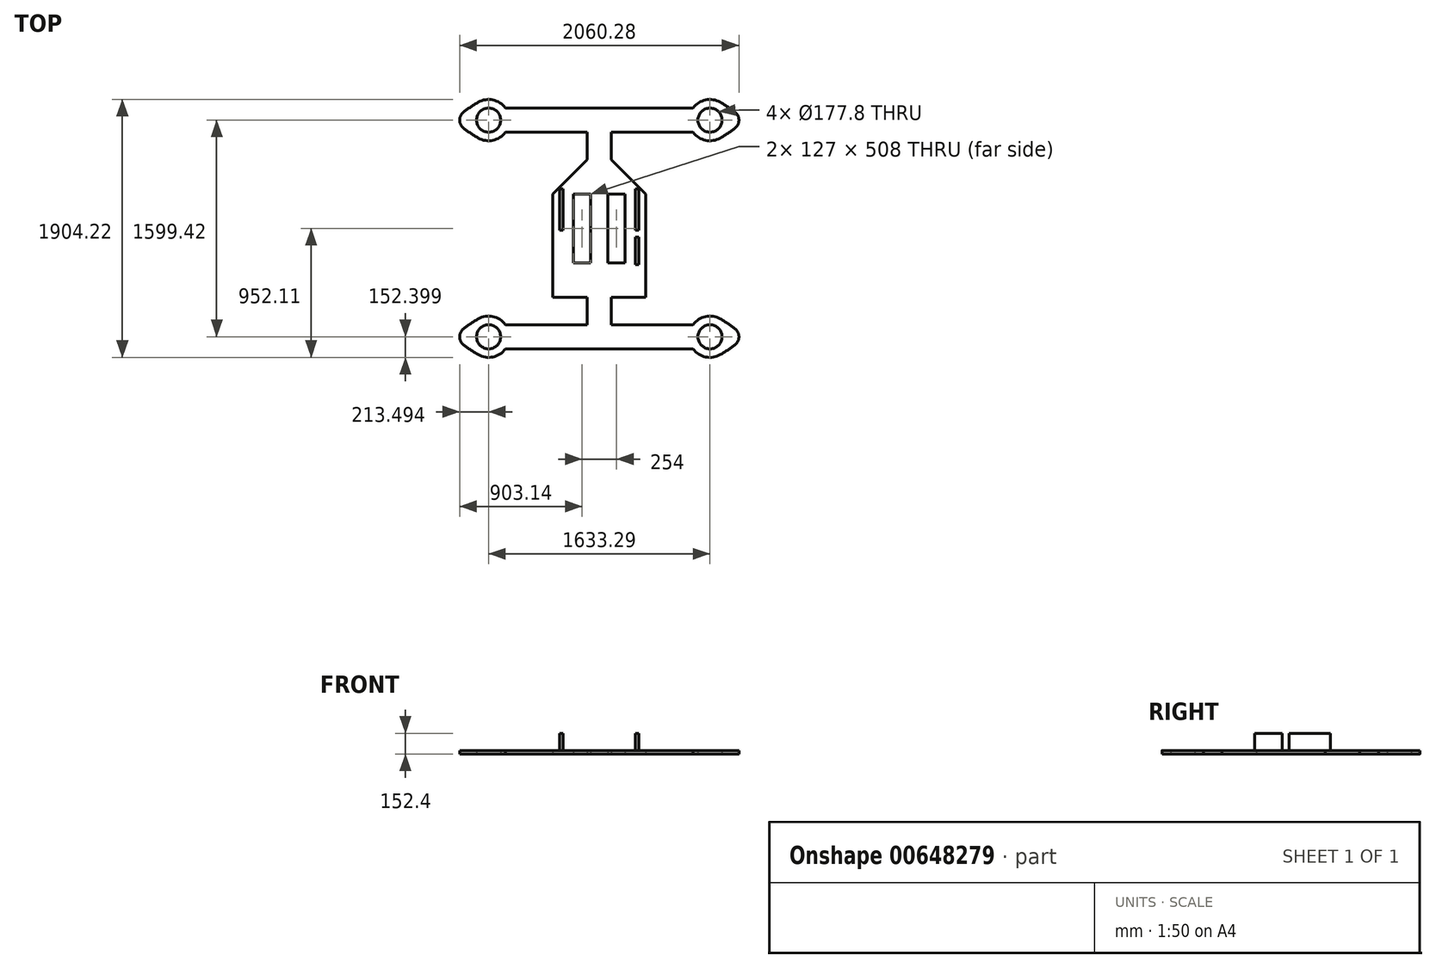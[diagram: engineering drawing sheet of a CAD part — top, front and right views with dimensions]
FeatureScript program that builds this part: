
annotation { "Feature Type Name" : "Feature", "Feature Type Description" : "" }
export const myFeature = defineFeature(function(context is Context, id is Id, definition is map)
    precondition{}
    {
        {
            var Q0;
            Q0=qCreatedBy(makeId("Top.planeOp"),FACE);
            var sketch = newSketch(context, id + "F0", { "sketchPlane" : qUnion([Q0])});
            skLineSegment(sketch, "E0.bottom", {"start": v(-816.65, 799.71) * mm, "end": v(816.65, 799.71) * mm, "construction": true});
            skLineSegment(sketch, "E0.top", {"start": v(-816.65, -799.71) * mm, "end": v(816.65, -799.71) * mm, "construction": true});
            skLineSegment(sketch, "E0.left", {"start": v(-816.65, 799.71) * mm, "end": v(-816.65, -799.71) * mm, "construction": true});
            skLineSegment(sketch, "E0.right", {"start": v(816.65, 799.71) * mm, "end": v(816.65, -799.71) * mm, "construction": true});
            skCircle(sketch, "E1", {"center": v(-816.65, 799.71) * mm, "radius": 88.9 * mm});
            skCircle(sketch, "E2", {"center": v(816.65, 799.71) * mm, "radius": 88.9 * mm});
            skCircle(sketch, "E3", {"center": v(816.65, -799.71) * mm, "radius": 88.9 * mm});
            skCircle(sketch, "E4", {"center": v(-816.65, -799.71) * mm, "radius": 88.9 * mm});
            skArc(sketch, "E5", {"start": v(-892.85, 667.73) * mm, "mid": v(-784.55, 650.73) * mm, "end": v(-692.86, 710.81) * mm});
            skArc(sketch, "E6", {"start": v(892.85, 931.7) * mm, "mid": v(784.55, 948.7) * mm, "end": v(692.86, 888.61) * mm});
            skArc(sketch, "E7", {"start": v(892.85, -667.73) * mm, "mid": v(784.55, -650.73) * mm, "end": v(692.86, -710.81) * mm});
            skArc(sketch, "E8", {"start": v(-892.85, -931.7) * mm, "mid": v(-784.55, -948.7) * mm, "end": v(-692.86, -888.61) * mm});
            skPoint(sketch, "E9.endSnap0", {"position": v(816.65, 0) * mm});
            skLineSegment(sketch, "E10", {"start": v(-692.86, 888.61) * mm, "end": v(692.86, 888.61) * mm});
            skLineSegment(sketch, "E11", {"start": v(-692.86, -888.61) * mm, "end": v(692.86, -888.61) * mm});
            skLineSegment(sketch, "E12.top", {"start": v(-342.9, -508) * mm, "end": v(-88.9, -508) * mm});
            skLineSegment(sketch, "E12.left", {"start": v(-342.9, 254) * mm, "end": v(-342.9, -508) * mm});
            skLineSegment(sketch, "E12.right", {"start": v(342.9, 254) * mm, "end": v(342.9, -508) * mm});
            skLineSegment(sketch, "E13", {"start": v(-88.9, 710.81) * mm, "end": v(-88.9, 508) * mm});
            skPoint(sketch, "E13.endSnap0", {"position": v(0, 508) * mm});
            skLineSegment(sketch, "E14", {"start": v(-88.9, -508) * mm, "end": v(-88.9, -710.81) * mm});
            skLineSegment(sketch, "E15", {"start": v(-88.9, 710.81) * mm, "end": v(-692.86, 710.81) * mm});
            skLineSegment(sketch, "E16", {"start": v(-88.9, -710.81) * mm, "end": v(-692.86, -710.81) * mm});
            skLineSegment(sketch, "E17", {"start": v(0, 0) * mm, "end": v(342.9, 0) * mm, "construction": true});
            skLineSegment(sketch, "E18", {"start": v(0, 0) * mm, "end": v(0, 1037.77) * mm, "construction": true});
            skLineSegment(sketch, "E19.MirrorCS", {"start": v(88.9, 710.81) * mm, "end": v(88.9, 508) * mm});
            skLineSegment(sketch, "E20.MirrorCS", {"start": v(88.9, 710.81) * mm, "end": v(692.86, 710.81) * mm});
            skLineSegment(sketch, "E21.MirrorCS", {"start": v(88.9, -710.81) * mm, "end": v(692.86, -710.81) * mm});
            skLineSegment(sketch, "E22.MirrorCS", {"start": v(88.9, -508) * mm, "end": v(88.9, -710.81) * mm});
            skLineSegment(sketch, "E23.trimOffspring", {"start": v(88.9, -508) * mm, "end": v(342.9, -508) * mm});
            skArc(sketch, "E24", {"start": v(1000.09, 860.35) * mm, "mid": v(947.6, 897.72) * mm, "end": v(892.85, 931.7) * mm});
            skArc(sketch, "E25", {"start": v(892.85, 667.73) * mm, "mid": v(947.6, 701.7) * mm, "end": v(1000.09, 739.07) * mm});
            skPoint(sketch, "E26.visualSharp", {"position": v(1072.53, 799.71) * mm});
            skArc(sketch, "E26.filletArc", {"start": v(1000.09, 739.07) * mm, "mid": v(1030.14, 799.71) * mm, "end": v(1000.09, 860.35) * mm});
            skArc(sketch, "E27.MirrorCS", {"start": v(-892.85, 667.73) * mm, "mid": v(-947.6, 701.7) * mm, "end": v(-1000.09, 739.07) * mm});
            skArc(sketch, "E28.MirrorCS", {"start": v(-1000.09, 739.07) * mm, "mid": v(-1030.14, 799.71) * mm, "end": v(-1000.09, 860.35) * mm});
            skArc(sketch, "E29.MirrorCS", {"start": v(-1000.09, 860.35) * mm, "mid": v(-947.6, 897.72) * mm, "end": v(-892.85, 931.7) * mm});
            skArc(sketch, "E30.MirrorCS", {"start": v(1000.09, -860.35) * mm, "mid": v(947.6, -897.72) * mm, "end": v(892.85, -931.7) * mm});
            skArc(sketch, "E31.MirrorCS", {"start": v(1000.09, -739.07) * mm, "mid": v(1030.14, -799.71) * mm, "end": v(1000.09, -860.35) * mm});
            skArc(sketch, "E32.MirrorCS", {"start": v(892.85, -667.73) * mm, "mid": v(947.6, -701.7) * mm, "end": v(1000.09, -739.07) * mm});
            skArc(sketch, "E33.MirrorCS", {"start": v(-1000.09, -860.35) * mm, "mid": v(-947.6, -897.72) * mm, "end": v(-892.85, -931.7) * mm});
            skArc(sketch, "E34.MirrorCS", {"start": v(-1000.09, -739.07) * mm, "mid": v(-1030.14, -799.71) * mm, "end": v(-1000.09, -860.35) * mm});
            skArc(sketch, "E35.MirrorCS", {"start": v(-892.85, -667.73) * mm, "mid": v(-947.6, -701.7) * mm, "end": v(-1000.09, -739.07) * mm});
            skLineSegment(sketch, "E36.bottom", {"start": v(-190.5, 254) * mm, "end": v(-63.5, 254) * mm});
            skLineSegment(sketch, "E36.top", {"start": v(-190.5, -254) * mm, "end": v(-63.5, -254) * mm});
            skLineSegment(sketch, "E36.left", {"start": v(-190.5, 254) * mm, "end": v(-190.5, -254) * mm});
            skLineSegment(sketch, "E36.right", {"start": v(-63.5, 254) * mm, "end": v(-63.5, -254) * mm});
            skLineSegment(sketch, "E37.bottom", {"start": v(63.5, 254) * mm, "end": v(190.5, 254) * mm});
            skLineSegment(sketch, "E37.top", {"start": v(63.5, -254) * mm, "end": v(190.5, -254) * mm});
            skLineSegment(sketch, "E37.left", {"start": v(63.5, 254) * mm, "end": v(63.5, -254) * mm});
            skLineSegment(sketch, "E37.right", {"start": v(190.5, 254) * mm, "end": v(190.5, -254) * mm});
            skLineSegment(sketch, "E38", {"start": v(88.9, 508) * mm, "end": v(342.9, 254) * mm});
            skLineSegment(sketch, "E39", {"start": v(-88.9, 508) * mm, "end": v(-342.9, 254) * mm});
            skPoint(sketch, "E40.orphan", {"position": v(-342.9, 508) * mm});
            skPoint(sketch, "E41.orphan", {"position": v(342.9, 508) * mm});
            skLineSegment(sketch, "E42.trimOffspring", {"start": v(816.65, 0) * mm, "end": v(1418.73, 0) * mm, "construction": true});
            skArc(sketch, "E43.trimOffspring", {"start": v(-692.86, 888.61) * mm, "mid": v(-784.55, 948.7) * mm, "end": v(-892.85, 931.7) * mm});
            skArc(sketch, "E44.trimOffspring", {"start": v(692.86, 710.81) * mm, "mid": v(784.55, 650.73) * mm, "end": v(892.85, 667.73) * mm});
            skArc(sketch, "E45.trimOffspring", {"start": v(692.86, -888.61) * mm, "mid": v(784.55, -948.7) * mm, "end": v(892.85, -931.7) * mm});
            skArc(sketch, "E46.trimOffspring", {"start": v(-692.86, -710.81) * mm, "mid": v(-784.55, -650.73) * mm, "end": v(-892.85, -667.73) * mm});
            skSolve(sketch);
        }
        {
            var Q0;
            Q0 = qSketchRegion(id + "F0", true);
            extrude(context, id + "F1", {"entities" : qUnion([Q0]), "depth" : 25.4 * mm, "offsetDistance" : 25.4 * mm});
        }
        {
            var Q0;
            Q0=makeQuery(id+"F1.opExtrude","CAP_FACE",FACE,{"disambiguationData":[OSD([sQuery(id+"F0.wireOp",EDGE,"E1"),sQuery(id+"F0.wireOp",EDGE,"E2"),sQuery(id+"F0.wireOp",EDGE,"E3"),sQuery(id+"F0.wireOp",EDGE,"E4"),sQuery(id+"F0.wireOp",EDGE,"E5"),sQuery(id+"F0.wireOp",EDGE,"E6"),sQuery(id+"F0.wireOp",EDGE,"E7"),sQuery(id+"F0.wireOp",EDGE,"E8"),sQuery(id+"F0.wireOp",EDGE,"E10"),sQuery(id+"F0.wireOp",EDGE,"E11"),sQuery(id+"F0.wireOp",EDGE,"E12.top"),sQuery(id+"F0.wireOp",EDGE,"E12.left"),sQuery(id+"F0.wireOp",EDGE,"E12.right"),sQuery(id+"F0.wireOp",EDGE,"E13"),sQuery(id+"F0.wireOp",EDGE,"E14"),sQuery(id+"F0.wireOp",EDGE,"E15"),sQuery(id+"F0.wireOp",EDGE,"E16"),sQuery(id+"F0.wireOp",EDGE,"E19.MirrorCS"),sQuery(id+"F0.wireOp",EDGE,"E20.MirrorCS"),sQuery(id+"F0.wireOp",EDGE,"E21.MirrorCS"),sQuery(id+"F0.wireOp",EDGE,"E22.MirrorCS"),sQuery(id+"F0.wireOp",EDGE,"E23.trimOffspring"),sQuery(id+"F0.wireOp",EDGE,"E24"),sQuery(id+"F0.wireOp",EDGE,"E25"),sQuery(id+"F0.wireOp",EDGE,"E26.filletArc"),sQuery(id+"F0.wireOp",EDGE,"E29.MirrorCS"),sQuery(id+"F0.wireOp",EDGE,"E28.MirrorCS"),sQuery(id+"F0.wireOp",EDGE,"E27.MirrorCS"),sQuery(id+"F0.wireOp",EDGE,"E30.MirrorCS"),sQuery(id+"F0.wireOp",EDGE,"E31.MirrorCS"),sQuery(id+"F0.wireOp",EDGE,"E32.MirrorCS"),sQuery(id+"F0.wireOp",EDGE,"E33.MirrorCS"),sQuery(id+"F0.wireOp",EDGE,"E34.MirrorCS"),sQuery(id+"F0.wireOp",EDGE,"E35.MirrorCS"),sQuery(id+"F0.wireOp",EDGE,"E36.bottom"),sQuery(id+"F0.wireOp",EDGE,"E36.top"),sQuery(id+"F0.wireOp",EDGE,"E36.left"),sQuery(id+"F0.wireOp",EDGE,"E36.right"),sQuery(id+"F0.wireOp",EDGE,"E37.bottom"),sQuery(id+"F0.wireOp",EDGE,"E37.top"),sQuery(id+"F0.wireOp",EDGE,"E37.left"),sQuery(id+"F0.wireOp",EDGE,"E37.right"),sQuery(id+"F0.wireOp",EDGE,"E38"),sQuery(id+"F0.wireOp",EDGE,"E39"),sQuery(id+"F0.wireOp",EDGE,"E43.trimOffspring"),sQuery(id+"F0.wireOp",EDGE,"E44.trimOffspring"),sQuery(id+"F0.wireOp",EDGE,"E45.trimOffspring"),sQuery(id+"F0.wireOp",EDGE,"E46.trimOffspring")])],"isStart":false});
            var sketch = newSketch(context, id + "F2", { "sketchPlane" : qUnion([Q0])});
            skLineSegment(sketch, "E47.bottom", {"start": v(-292.1, 444.5) * mm, "end": v(292.1, 444.5) * mm, "construction": true});
            skLineSegment(sketch, "E47.left", {"start": v(-292.1, 444.5) * mm, "end": v(-292.1, -12.7) * mm, "construction": true});
            skLineSegment(sketch, "E47.right", {"start": v(292.1, 444.5) * mm, "end": v(292.1, -12.7) * mm, "construction": true});
            skLineSegment(sketch, "E48", {"start": v(0, 888.61) * mm, "end": v(0, -888.61) * mm});
            skLineSegment(sketch, "E49", {"start": v(0, 0) * mm, "end": v(-1720.82, 0) * mm});
            skLineSegment(sketch, "E50.bottom", {"start": v(-292.1, -12.7) * mm, "end": v(-266.7, -12.7) * mm});
            skLineSegment(sketch, "E50.top", {"start": v(-292.1, 292.1) * mm, "end": v(-266.7, 292.1) * mm});
            skLineSegment(sketch, "E50.left", {"start": v(-292.1, -12.7) * mm, "end": v(-292.1, 292.1) * mm});
            skLineSegment(sketch, "E50.right", {"start": v(-266.7, -12.7) * mm, "end": v(-266.7, 292.1) * mm});
            skLineSegment(sketch, "E51.bottom", {"start": v(292.1, -12.7) * mm, "end": v(266.7, -12.7) * mm});
            skLineSegment(sketch, "E51.top", {"start": v(292.1, 292.1) * mm, "end": v(266.7, 292.1) * mm});
            skLineSegment(sketch, "E51.left", {"start": v(292.1, -12.7) * mm, "end": v(292.1, 292.1) * mm});
            skLineSegment(sketch, "E51.right", {"start": v(266.7, -12.7) * mm, "end": v(266.7, 292.1) * mm});
            skLineSegment(sketch, "E52.bottom", {"start": v(292.1, -266.7) * mm, "end": v(266.7, -266.7) * mm});
            skLineSegment(sketch, "E52.top", {"start": v(292.1, -63.5) * mm, "end": v(266.7, -63.5) * mm});
            skLineSegment(sketch, "E52.left", {"start": v(292.1, -266.7) * mm, "end": v(292.1, -63.5) * mm});
            skLineSegment(sketch, "E52.right", {"start": v(266.7, -266.7) * mm, "end": v(266.7, -63.5) * mm});
            skLineSegment(sketch, "E53.trimOffspring", {"start": v(266.7, 292.1) * mm, "end": v(292.1, 292.1) * mm});
            skLineSegment(sketch, "E54.trimOffspring", {"start": v(292.1, -63.5) * mm, "end": v(292.1, -266.7) * mm, "construction": true});
            skSolve(sketch);
        }
        {
            var Q0;
            Q0 = qSketchRegion(id + "F2", true);
            extrude(context, id + "F3", {"entities" : qUnion([Q0]), "operationType" : NewBodyOperationType.ADD, "depth" : 127 * mm, "offsetDistance" : 25.4 * mm});
        }
    });
